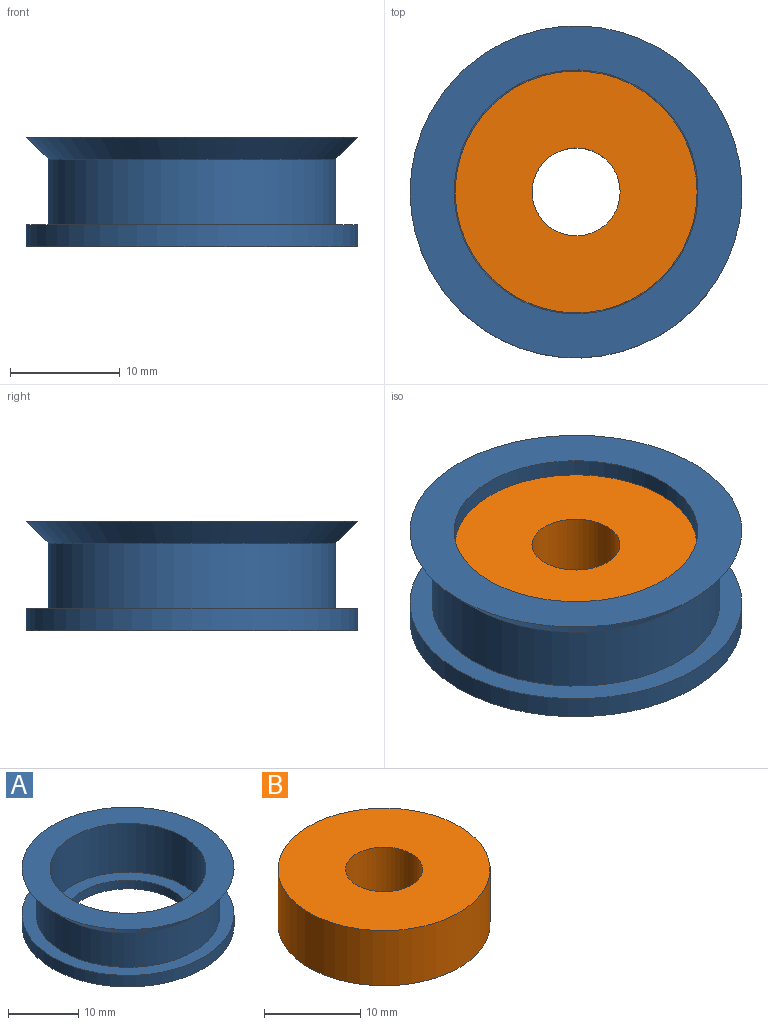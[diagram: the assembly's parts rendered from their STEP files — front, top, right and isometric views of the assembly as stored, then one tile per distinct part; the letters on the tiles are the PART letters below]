
ASSEMBLY  parts=2 mates=1
PART A: 9 faces, bbox 30.2x30.2x10 mm
  f0: plane 30.2x30.2mm, normal (0,0,1), area 329.2mm2, adj f1,f8
  f1: cylinder r=11.1mm len=22.2mm, axis (0,0,-1), area 592.8mm2, adj f0,f2
  f2: plane 22.2x22.2mm, normal (0,0,1), area 126.9mm2, adj f1,f3
  f3: cylinder r=9.1mm len=18.2mm, axis (0,0,-1), area 85.8mm2, adj f2,f4
  f4: plane 30.2x30.2mm, normal (0,0,-1), area 456.2mm2, adj f3,f5
  f5: cylinder r=15.1mm len=30.2mm, axis (0,0,-1), area 189.8mm2, adj f4,f6
  f6: plane 30.2x30.2mm, normal (0,0,1), area 177.2mm2, adj f5,f7
  f7: cylinder r=13.1mm len=26.2mm, axis (0,0,-1), area 493.9mm2, adj f6,f8
  f8: cone r=15.1mm half-angle=45deg, axis (0,0,1), area 250.6mm2, adj f0,f7
PART B: 4 faces, bbox 22x22x7 mm
  f0: cylinder r=4mm len=8mm, axis (0,0,-1), area 175.9mm2, adj f2,f3
  f1: cylinder r=11mm len=22mm, axis (0,0,-1), area 483.8mm2, adj f2,f3
  f2: plane 22x22mm, normal (0,0,1), area 329.9mm2, adj f0,f1
  f3: plane 22x22mm, normal (0,0,-1), area 329.9mm2, adj f0,f1
PLACE A t=(4.74,5.32,1.07)mm
PLACE B rot(axis=(1,0,0),180deg) t=(4.74,5.32,4.38)mm
MATE fastened B.f0 <-> A.f1  axis (0,0,1) through (4.74,5.32,-2.62)mm
